# Revit family: IHLS-L-324-570-840-x
name_source: partatom
category: Leuchten
revit_build: Autodesk Revit 2017 (Build: 20190508_0315(x64)
units: mm (PartAtom-declared; Revit-internal decimal feet)

## family parameters
Basisbauteil = Fläche
Beim Laden mit Abzugskörper schneiden = Nein
Bemaßung runder Anschluss = Durchmesser verwenden
Gemeinsam genutzt = Nein
Lichtquelle = Ja
OmniClass-Nummer = 23.80.70.11
OmniClass-Titel = Luminaries for Internal Lighting
Raumberechnungspunkt = Nein
Teiletyp = Normal

## types (8) — shared parameters
Baugruppenkennzeichen = D5020200
Emissionsform beim Rendern sichtbar = Nein
Farbfilter = 16777215
Farbtemperaturverschiebung bei Dämpfen der Lampe = <Keine Auswahl>
Hersteller = RIDI Leuchten GmbH
Lampe = LED
Neigungswinkel = 90.00°
Scheinlast = 45 VA
URL = www.ridi.de
Von Breite des Rechtecks ausssenden = 574 mm  [stored 1.8832 ft]
Von Länge des Rechtecks aussenden = 574 mm  [stored 1.8832 ft]
brand = RIDI
conformity mark = CE
electrical safety class = 1
height = 80 mm  [stored 0.262467 ft]
ingress protection (IP) code = IP64
length = 600 mm
nominal frequency = 50-60Hz
nominal voltage = 230
rated input power = 45
voltage type (AC, DC, UC) = AC
width = 600 mm
zero-valued in all types: Vorgabe-Ansicht

## per-type parameters (varying)
| type | Datei für fotometrisches Netz | Modell | weight |
| IHLS-L 324-570-840 SM | IHLS-L 324570-840 SM.IES | 0650557 | 9,4 kg |
| IHLS-L 324-570-840 SM-DA | IHLS-L 324570-840 SM.IES | 0660557 | 9,4 kg |
| IHLS-L 324-570-840 SB | IHLS-L 324570-840 SB.IES | 0650081 | 7,3 kg |
| IHLS-L 324-570-840 SB-DA | IHLS-L 324570-840 SB.IES | 0660081 | 7,3 kg |
| IHLS-L 324-570-840 OS | IHLS-L 324570-840 OS.IES | 0650091 | 7,3 kg |
| IHLS-L 324-570-840 OS-DA | IHLS-L 324570-840 OS.IES | 0660091 | 7,3 kg |
| IHLS-L 324-570-840 W | IHLS-L 324570-840 W.IES | 0650071 | 9,4 kg |
| IHLS-L 324-570-840 W-DA | IHLS-L 324570-840 W.IES | 0660071 | 9,4 kg |

note: column(s) folded — value = type name in every type: product name

note: [stored X ft] marks values corroborated as IEEE doubles in the binary element streams (Revit-internal decimal feet)
